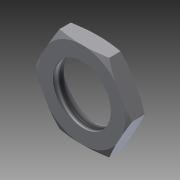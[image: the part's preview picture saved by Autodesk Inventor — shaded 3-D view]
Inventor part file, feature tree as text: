
AUTODESK INVENTOR PART (.ipt)
format: ipt  version: 2011 SP1 (Build 150282100, 282)  size: 120,320 bytes
history: native  units: in
note: dims shown in document units (in); Inventor stores cm internally (conversion verified against a paired STEP export)
features: other x7, sketch x3, revolve x1, extrude x1, hole x1
ambient origin geometry x8: Origin, YZ Plane, XZ Plane, XY Plane, X Axis, Y Axis, Z Axis, Center Point
bodies: Solid1 (feature_tree)
feature tree (13):
  revolve  "Revolution1"  [1 undecoded]
  extrude  "Extrusion1"  [1 undecoded]
  hole  "Drilling 1"  [1 undecoded]
  other  "nut_XY"
  other  "nut_YZ"
  other  "nut_ZX"
  other  "nut_X"
  other  "nut_Y"
  other  "nut_Z"
  other  "nut_Center"
  sketch  "Sketch_1"  dims[d0=360.0deg d1=0.118in d2=0.0in]
  sketch  "Sketch_2"  dims[d3=0.211in d4=0.059in d5=0.25in d6=0.25in d7=0.6184in d8=0.059in d9=0.0in]
  sketch  "Sketch3"
note: 3 required parameter values undecoded (feature->parameter linkage not recoverable at this tier; creation-order binding heuristic only, values carry confidence <= 0.55)